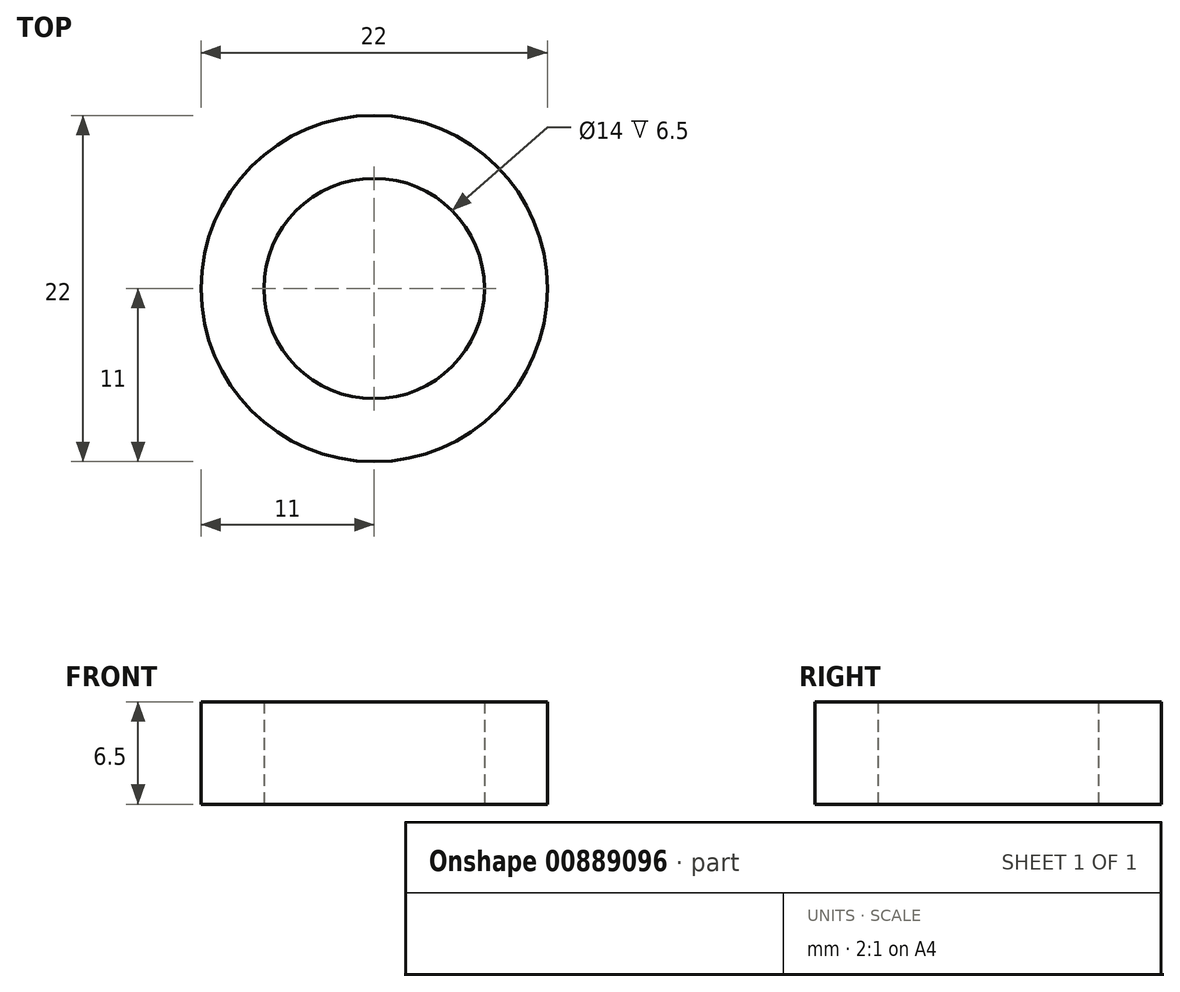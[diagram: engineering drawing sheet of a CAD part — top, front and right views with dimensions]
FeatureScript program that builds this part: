
annotation { "Feature Type Name" : "Feature", "Feature Type Description" : "" }
export const myFeature = defineFeature(function(context is Context, id is Id, definition is map)
    precondition{}
    {
        {
            var Q0;
            Q0=qCreatedBy(makeId("Top.planeOp"),FACE);
            var sketch = newSketch(context, id + "F0", { "sketchPlane" : qUnion([Q0])});
            skCircle(sketch, "E0", {"center": v(0, 0) * mm, "radius": 7 * mm});
            skCircle(sketch, "E1", {"center": v(0, 0) * mm, "radius": 11 * mm});
            skSolve(sketch);
        }
        {
            var Q0;
            Q0=makeQuery(id+"F0.imprint","IMPRINT",FACE,{"disambiguationData":[TD([[makeQuery(id+"F0.imprint","IMPRINT",EDGE,{"derivedFrom":sQuery(id+"F0.wireOp",EDGE,"E0")}),-1.0]])]});
            extrude(context, id + "F1", {"entities" : qUnion([Q0]), "depth" : 6.5 * mm, "offsetDistance" : 25 * mm});
        }
    });
